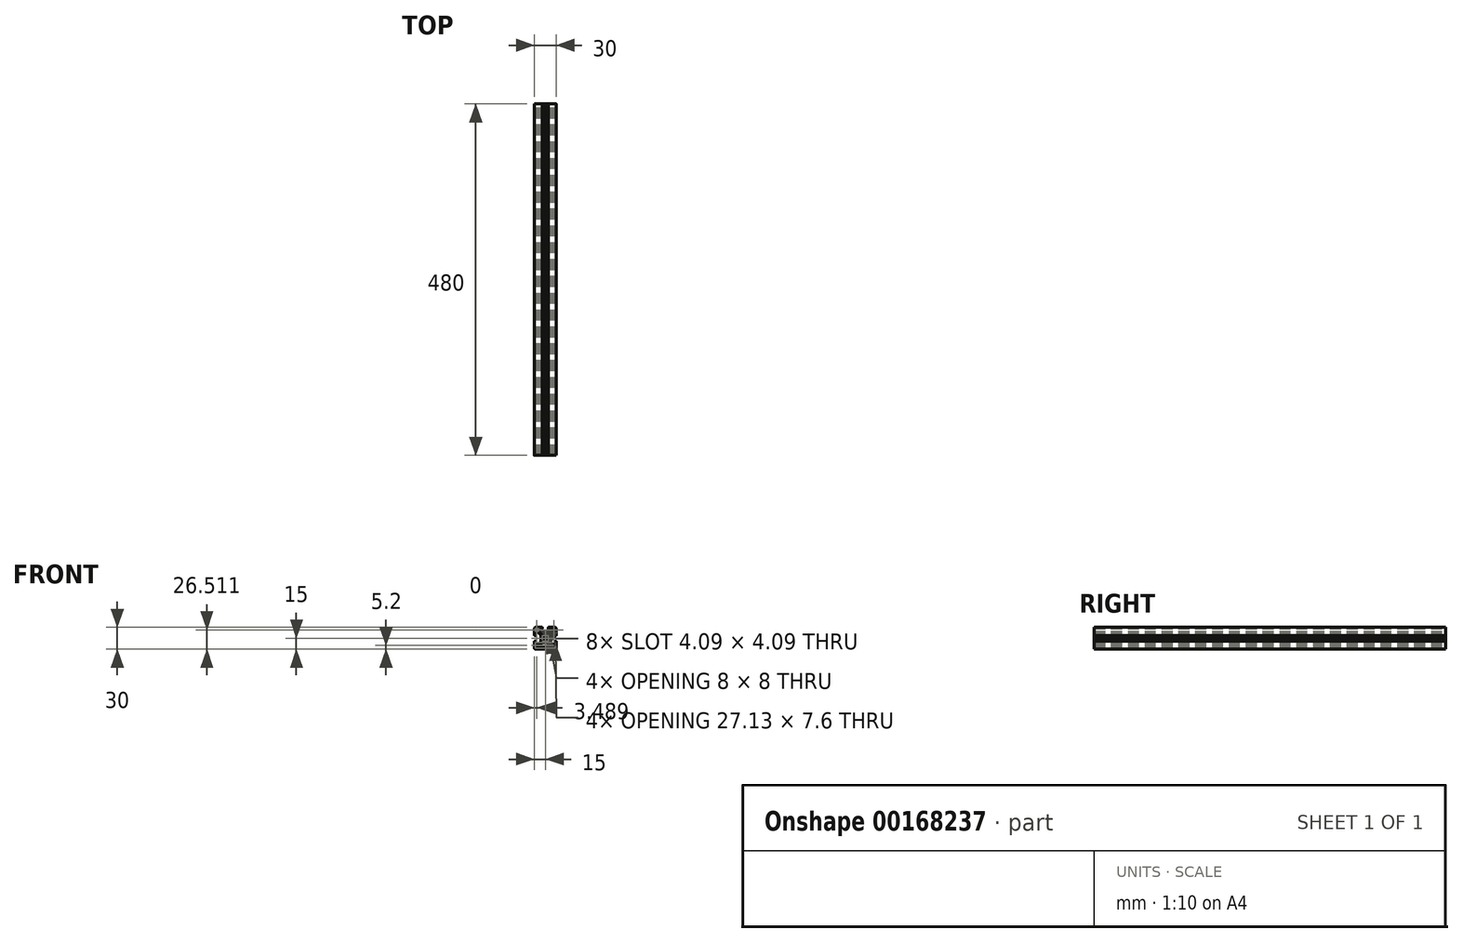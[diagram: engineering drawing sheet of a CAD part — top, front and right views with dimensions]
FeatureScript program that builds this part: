
annotation { "Feature Type Name" : "Feature", "Feature Type Description" : "" }
export const myFeature = defineFeature(function(context is Context, id is Id, definition is map)
    precondition{}
    {
        {
            var Q0;
            Q0=qCreatedBy(makeId("Front.planeOp"),FACE);
            var sketch = newSketch(context, id + "F0", { "sketchPlane" : qUnion([Q0])});
            skLineSegment(sketch, "E0", {"start": v(0, 17) * mm, "end": v(0, -17) * mm});
            skLineSegment(sketch, "E1", {"start": v(-17, 0) * mm, "end": v(17, 0) * mm});
            skLineSegment(sketch, "E2", {"start": v(-13, 15) * mm, "end": v(-4.3, 15) * mm});
            skLineSegment(sketch, "E3", {"start": v(-13, -15) * mm, "end": v(13, -15) * mm});
            skLineSegment(sketch, "E4", {"start": v(-15, 13) * mm, "end": v(-15, 4.3) * mm});
            skArc(sketch, "E5", {"start": v(15, 13) * mm, "mid": v(14.41, 14.41) * mm, "end": v(13, 15) * mm});
            skArc(sketch, "E6", {"start": v(-13, 15) * mm, "mid": v(-14.41, 14.41) * mm, "end": v(-15, 13) * mm});
            skArc(sketch, "E7", {"start": v(-15, -13) * mm, "mid": v(-14.41, -14.41) * mm, "end": v(-13, -15) * mm});
            skArc(sketch, "E8", {"start": v(13, -15) * mm, "mid": v(14.41, -14.41) * mm, "end": v(15, -13) * mm});
            skLineSegment(sketch, "E9", {"start": v(-13, -8.25) * mm, "end": v(-13, -4.3) * mm});
            skLineSegment(sketch, "E10", {"start": v(-8.08, -13) * mm, "end": v(8.08, -13) * mm});
            skLineSegment(sketch, "E11", {"start": v(-14.7, -4) * mm, "end": v(-13.3, -4) * mm});
            skLineSegment(sketch, "E12", {"start": v(-14.7, 4) * mm, "end": v(-13.3, 4) * mm});
            skLineSegment(sketch, "E13", {"start": v(-13, 4.3) * mm, "end": v(-13, 8.25) * mm});
            skLineSegment(sketch, "E14", {"start": v(4.3, 15) * mm, "end": v(13, 15) * mm});
            skLineSegment(sketch, "E15", {"start": v(-9.66, -8.25) * mm, "end": v(-13, -8.25) * mm});
            skLineSegment(sketch, "E16", {"start": v(-9.66, 8.25) * mm, "end": v(-13, 8.25) * mm});
            skLineSegment(sketch, "E17", {"start": v(4.59, 6) * mm, "end": v(0.65, 6) * mm});
            skLineSegment(sketch, "E18", {"start": v(4.17, -6) * mm, "end": v(-4.17, -6) * mm});
            skLineSegment(sketch, "E19", {"start": v(-6, -4.59) * mm, "end": v(-6, -2.5) * mm});
            skLineSegment(sketch, "E20", {"start": v(-4.59, 6) * mm, "end": v(-8.25, 9.66) * mm});
            skLineSegment(sketch, "E21", {"start": v(-6, 4.59) * mm, "end": v(-9.66, 8.25) * mm});
            skLineSegment(sketch, "E22", {"start": v(4.59, 6) * mm, "end": v(8.25, 9.66) * mm});
            skLineSegment(sketch, "E23", {"start": v(4.88, -6.3) * mm, "end": v(7.74, -9.16) * mm});
            skLineSegment(sketch, "E24", {"start": v(-4.88, -6.3) * mm, "end": v(-7.74, -9.16) * mm});
            skLineSegment(sketch, "E25", {"start": v(-6, -4.59) * mm, "end": v(-9.66, -8.25) * mm});
            skLineSegment(sketch, "E26", {"start": v(-15, -4.3) * mm, "end": v(-15, -13) * mm});
            skLineSegment(sketch, "E27", {"start": v(-4, 14.7) * mm, "end": v(-4, 13.3) * mm});
            skLineSegment(sketch, "E28", {"start": v(4, 14.7) * mm, "end": v(4, 13.3) * mm});
            skLineSegment(sketch, "E29", {"start": v(8.25, 9.66) * mm, "end": v(8.25, 13) * mm});
            skLineSegment(sketch, "E30", {"start": v(-8.25, 9.66) * mm, "end": v(-8.25, 13) * mm});
            skLineSegment(sketch, "E31", {"start": v(-4.3, 13) * mm, "end": v(-8.25, 13) * mm});
            skLineSegment(sketch, "E32", {"start": v(4.3, 13) * mm, "end": v(8.25, 13) * mm});
            skArc(sketch, "E33", {"start": v(-9.91, 12.35) * mm, "mid": v(-13.04, 13.04) * mm, "end": v(-12.35, 9.91) * mm});
            skLineSegment(sketch, "E34", {"start": v(-9.55, 11.34) * mm, "end": v(-9.91, 12.35) * mm});
            skLineSegment(sketch, "E35", {"start": v(-11.34, 9.55) * mm, "end": v(-12.35, 9.91) * mm});
            skArc(sketch, "E36", {"start": v(-11.34, 9.55) * mm, "mid": v(-9.87, 9.87) * mm, "end": v(-9.55, 11.34) * mm});
            skLineSegment(sketch, "E37", {"start": v(-8.45, -9.45) * mm, "end": v(-11.07, -9.45) * mm});
            skLineSegment(sketch, "E38", {"start": v(-11.07, -9.45) * mm, "end": v(-12.35, -9.91) * mm});
            skArc(sketch, "E39", {"start": v(-12.35, -9.91) * mm, "mid": v(-13.2, -12.86) * mm, "end": v(-10.14, -12.78) * mm});
            skArc(sketch, "E40", {"start": v(-8.5, -12.78) * mm, "mid": v(-9.31, -12.35) * mm, "end": v(-10.14, -12.78) * mm});
            skArc(sketch, "E41", {"start": v(-8.45, -9.45) * mm, "mid": v(-8.07, -9.37) * mm, "end": v(-7.74, -9.16) * mm});
            skArc(sketch, "E42", {"start": v(-4.17, -6) * mm, "mid": v(-4.55, -6.08) * mm, "end": v(-4.88, -6.3) * mm});
            skArc(sketch, "E43", {"start": v(4.88, -6.3) * mm, "mid": v(4.55, -6.08) * mm, "end": v(4.17, -6) * mm});
            skLineSegment(sketch, "E44", {"start": v(3.5, 4) * mm, "end": v(2, 4) * mm});
            skLineSegment(sketch, "E45", {"start": v(4, -3.5) * mm, "end": v(4, -2) * mm});
            skLineSegment(sketch, "E46", {"start": v(3.5, -4) * mm, "end": v(2, -4) * mm});
            skLineSegment(sketch, "E47", {"start": v(-4, -3.5) * mm, "end": v(-4, -2) * mm});
            skLineSegment(sketch, "E48", {"start": v(-2.5, 6) * mm, "end": v(-1.22, 5.75) * mm});
            skLineSegment(sketch, "E49", {"start": v(0, 5.7) * mm, "end": v(-0.4, 5.93) * mm});
            skLineSegment(sketch, "E50", {"start": v(0, 5.7) * mm, "end": v(0.4, 5.93) * mm});
            skLineSegment(sketch, "E51", {"start": v(-2.5, 6) * mm, "end": v(-4.59, 6) * mm});
            skArc(sketch, "E52", {"start": v(0.65, 6) * mm, "mid": v(0.52, 5.98) * mm, "end": v(0.4, 5.93) * mm});
            skArc(sketch, "E53", {"start": v(-0.4, 5.93) * mm, "mid": v(-0.65, 6) * mm, "end": v(-0.9, 5.93) * mm});
            skLineSegment(sketch, "E54", {"start": v(-1.22, 5.75) * mm, "end": v(-0.9, 5.93) * mm});
            skArc(sketch, "E55", {"start": v(-6, 0.65) * mm, "mid": v(-5.98, 0.52) * mm, "end": v(-5.93, 0.4) * mm});
            skLineSegment(sketch, "E56", {"start": v(-6, -2.5) * mm, "end": v(-5.75, -1.22) * mm});
            skLineSegment(sketch, "E57", {"start": v(-5.7, 0) * mm, "end": v(-5.93, -0.4) * mm});
            skLineSegment(sketch, "E58", {"start": v(-5.7, 0) * mm, "end": v(-5.93, 0.4) * mm});
            skArc(sketch, "E59", {"start": v(-5.93, -0.4) * mm, "mid": v(-6, -0.65) * mm, "end": v(-5.93, -0.9) * mm});
            skLineSegment(sketch, "E60", {"start": v(-5.75, -1.22) * mm, "end": v(-5.93, -0.9) * mm});
            skLineSegment(sketch, "E61", {"start": v(-6, 0.65) * mm, "end": v(-6, 4.59) * mm});
            skArc(sketch, "E62", {"start": v(4, 13.3) * mm, "mid": v(4.09, 13.09) * mm, "end": v(4.3, 13) * mm});
            skArc(sketch, "E63", {"start": v(4.3, 15) * mm, "mid": v(4.09, 14.91) * mm, "end": v(4, 14.7) * mm});
            skArc(sketch, "E64", {"start": v(-4.3, 13) * mm, "mid": v(-4.09, 13.09) * mm, "end": v(-4, 13.3) * mm});
            skArc(sketch, "E65", {"start": v(-4, 14.7) * mm, "mid": v(-4.09, 14.91) * mm, "end": v(-4.3, 15) * mm});
            skArc(sketch, "E66", {"start": v(-13.3, 4) * mm, "mid": v(-13.09, 4.09) * mm, "end": v(-13, 4.3) * mm});
            skArc(sketch, "E67", {"start": v(-15, 4.3) * mm, "mid": v(-14.91, 4.09) * mm, "end": v(-14.7, 4) * mm});
            skArc(sketch, "E68", {"start": v(-13, -4.3) * mm, "mid": v(-13.09, -4.09) * mm, "end": v(-13.3, -4) * mm});
            skArc(sketch, "E69", {"start": v(-14.7, -4) * mm, "mid": v(-14.91, -4.09) * mm, "end": v(-15, -4.3) * mm});
            skArc(sketch, "E70", {"start": v(0.99, 3.25) * mm, "mid": v(0, 3.4) * mm, "end": v(-0.99, 3.25) * mm});
            skArc(sketch, "E71", {"start": v(-1.5, 3.58) * mm, "mid": v(-1.32, 3.3) * mm, "end": v(-0.99, 3.25) * mm});
            skArc(sketch, "E72", {"start": v(-1.5, 3.58) * mm, "mid": v(-1.67, 3.88) * mm, "end": v(-2, 4) * mm});
            skArc(sketch, "E73", {"start": v(0.99, 3.25) * mm, "mid": v(1.32, 3.3) * mm, "end": v(1.5, 3.58) * mm});
            skArc(sketch, "E74", {"start": v(2, 4) * mm, "mid": v(1.67, 3.88) * mm, "end": v(1.5, 3.58) * mm});
            skLineSegment(sketch, "E75", {"start": v(-2, 4) * mm, "end": v(-3.5, 4) * mm});
            skArc(sketch, "E76", {"start": v(-3.5, 4) * mm, "mid": v(-3.85, 3.85) * mm, "end": v(-4, 3.5) * mm});
            skArc(sketch, "E77", {"start": v(4, 3.5) * mm, "mid": v(3.85, 3.85) * mm, "end": v(3.5, 4) * mm});
            skArc(sketch, "E78", {"start": v(3.5, -4) * mm, "mid": v(3.85, -3.85) * mm, "end": v(4, -3.5) * mm});
            skArc(sketch, "E79", {"start": v(-4, -3.5) * mm, "mid": v(-3.85, -3.85) * mm, "end": v(-3.5, -4) * mm});
            skArc(sketch, "E80", {"start": v(-3.25, 0.99) * mm, "mid": v(-3.4, 0) * mm, "end": v(-3.25, -0.99) * mm});
            skArc(sketch, "E81", {"start": v(-3.58, -1.5) * mm, "mid": v(-3.3, -1.32) * mm, "end": v(-3.25, -0.99) * mm});
            skArc(sketch, "E82", {"start": v(-3.58, -1.5) * mm, "mid": v(-3.88, -1.67) * mm, "end": v(-4, -2) * mm});
            skArc(sketch, "E83", {"start": v(-3.25, 0.99) * mm, "mid": v(-3.3, 1.32) * mm, "end": v(-3.58, 1.5) * mm});
            skArc(sketch, "E84", {"start": v(-4, 2) * mm, "mid": v(-3.88, 1.67) * mm, "end": v(-3.58, 1.5) * mm});
            skArc(sketch, "E85", {"start": v(3.25, -0.99) * mm, "mid": v(3.4, 0) * mm, "end": v(3.25, 0.99) * mm});
            skArc(sketch, "E86", {"start": v(3.58, 1.5) * mm, "mid": v(3.3, 1.32) * mm, "end": v(3.25, 0.99) * mm});
            skArc(sketch, "E87", {"start": v(3.58, 1.5) * mm, "mid": v(3.88, 1.67) * mm, "end": v(4, 2) * mm});
            skArc(sketch, "E88", {"start": v(3.25, -0.99) * mm, "mid": v(3.3, -1.32) * mm, "end": v(3.58, -1.5) * mm});
            skArc(sketch, "E89", {"start": v(4, -2) * mm, "mid": v(3.88, -1.67) * mm, "end": v(3.58, -1.5) * mm});
            skArc(sketch, "E90", {"start": v(-0.99, -3.25) * mm, "mid": v(0, -3.4) * mm, "end": v(0.99, -3.25) * mm});
            skArc(sketch, "E91", {"start": v(-0.99, -3.25) * mm, "mid": v(-1.32, -3.3) * mm, "end": v(-1.5, -3.58) * mm});
            skArc(sketch, "E92", {"start": v(-2, -4) * mm, "mid": v(-1.67, -3.88) * mm, "end": v(-1.5, -3.58) * mm});
            skArc(sketch, "E93", {"start": v(1.5, -3.58) * mm, "mid": v(1.32, -3.3) * mm, "end": v(0.99, -3.25) * mm});
            skArc(sketch, "E94", {"start": v(1.5, -3.58) * mm, "mid": v(1.67, -3.88) * mm, "end": v(2, -4) * mm});
            skLineSegment(sketch, "E95", {"start": v(4, 2) * mm, "end": v(4, 3.5) * mm});
            skLineSegment(sketch, "E96", {"start": v(-2, -4) * mm, "end": v(-3.5, -4) * mm});
            skLineSegment(sketch, "E97", {"start": v(-4, 2) * mm, "end": v(-4, 3.5) * mm});
            skCircle(sketch, "E98", {"center": v(0, 0) * mm, "radius": 3.4 * mm});
            skLineSegment(sketch, "E99", {"start": v(-11.7, -7.8) * mm, "end": v(-11.7, -15.6) * mm});
            skLineSegment(sketch, "E100", {"start": v(-15.6, -11.7) * mm, "end": v(-7.8, -11.7) * mm});
            skLineSegment(sketch, "E101", {"start": v(-11.7, 15.6) * mm, "end": v(-11.7, 7.8) * mm});
            skLineSegment(sketch, "E102", {"start": v(-15.6, 11.7) * mm, "end": v(-7.8, 11.7) * mm});
            skArc(sketch, "E103", {"start": v(7.74, -9.16) * mm, "mid": v(8.07, -9.37) * mm, "end": v(8.45, -9.45) * mm});
            skArc(sketch, "E104", {"start": v(12.35, 9.91) * mm, "mid": v(13.04, 13.04) * mm, "end": v(9.91, 12.35) * mm});
            skLineSegment(sketch, "E105", {"start": v(9.55, 11.34) * mm, "end": v(9.91, 12.35) * mm});
            skLineSegment(sketch, "E106", {"start": v(11.34, 9.55) * mm, "end": v(12.35, 9.91) * mm});
            skArc(sketch, "E107", {"start": v(9.55, 11.34) * mm, "mid": v(9.87, 9.87) * mm, "end": v(11.34, 9.55) * mm});
            skLineSegment(sketch, "E108", {"start": v(8.45, -9.45) * mm, "end": v(11.07, -9.45) * mm});
            skLineSegment(sketch, "E109", {"start": v(11.07, -9.45) * mm, "end": v(12.35, -9.91) * mm});
            skArc(sketch, "E110", {"start": v(10.14, -12.78) * mm, "mid": v(13.2, -12.86) * mm, "end": v(12.35, -9.91) * mm});
            skArc(sketch, "E111", {"start": v(10.14, -12.78) * mm, "mid": v(9.31, -12.35) * mm, "end": v(8.5, -12.78) * mm});
            skLineSegment(sketch, "E112", {"start": v(11.7, -7.8) * mm, "end": v(11.7, -15.6) * mm});
            skLineSegment(sketch, "E113", {"start": v(15.6, -11.7) * mm, "end": v(7.8, -11.7) * mm});
            skLineSegment(sketch, "E114", {"start": v(11.7, 15.6) * mm, "end": v(11.7, 7.8) * mm});
            skLineSegment(sketch, "E115", {"start": v(15.6, 11.7) * mm, "end": v(7.8, 11.7) * mm});
            skLineSegment(sketch, "E116", {"start": v(15, 13) * mm, "end": v(15, 4.3) * mm});
            skLineSegment(sketch, "E117", {"start": v(15, -4.3) * mm, "end": v(15, -13) * mm});
            skLineSegment(sketch, "E118", {"start": v(13, -8.25) * mm, "end": v(13, -4.3) * mm});
            skLineSegment(sketch, "E119", {"start": v(13, 4.3) * mm, "end": v(13, 8.25) * mm});
            skLineSegment(sketch, "E120", {"start": v(14.7, -4) * mm, "end": v(13.3, -4) * mm});
            skArc(sketch, "E121", {"start": v(13.3, -4) * mm, "mid": v(13.09, -4.09) * mm, "end": v(13, -4.3) * mm});
            skLineSegment(sketch, "E122", {"start": v(14.7, 4) * mm, "end": v(13.3, 4) * mm});
            skArc(sketch, "E123", {"start": v(14.7, 4) * mm, "mid": v(14.91, 4.09) * mm, "end": v(15, 4.3) * mm});
            skArc(sketch, "E124", {"start": v(13, 4.3) * mm, "mid": v(13.09, 4.09) * mm, "end": v(13.3, 4) * mm});
            skLineSegment(sketch, "E125", {"start": v(9.66, 8.25) * mm, "end": v(13, 8.25) * mm});
            skLineSegment(sketch, "E126", {"start": v(9.66, -8.25) * mm, "end": v(13, -8.25) * mm});
            skLineSegment(sketch, "E127", {"start": v(6, 4.59) * mm, "end": v(9.66, 8.25) * mm});
            skLineSegment(sketch, "E128", {"start": v(6, -4.59) * mm, "end": v(9.66, -8.25) * mm});
            skArc(sketch, "E129", {"start": v(15, -4.3) * mm, "mid": v(14.91, -4.09) * mm, "end": v(14.7, -4) * mm});
            skLineSegment(sketch, "E130", {"start": v(6, 4.59) * mm, "end": v(6, 2.5) * mm});
            skLineSegment(sketch, "E131", {"start": v(6, -0.65) * mm, "end": v(6, -4.59) * mm});
            skArc(sketch, "E132", {"start": v(6, -0.65) * mm, "mid": v(5.98, -0.52) * mm, "end": v(5.93, -0.4) * mm});
            skLineSegment(sketch, "E133", {"start": v(6, 2.5) * mm, "end": v(5.75, 1.22) * mm});
            skLineSegment(sketch, "E134", {"start": v(5.7, 0) * mm, "end": v(5.93, 0.4) * mm});
            skLineSegment(sketch, "E135", {"start": v(5.7, 0) * mm, "end": v(5.93, -0.4) * mm});
            skArc(sketch, "E136", {"start": v(5.93, 0.4) * mm, "mid": v(6, 0.65) * mm, "end": v(5.93, 0.9) * mm});
            skLineSegment(sketch, "E137", {"start": v(5.75, 1.22) * mm, "end": v(5.93, 0.9) * mm});
            skArc(sketch, "E138", {"start": v(8.08, -13) * mm, "mid": v(8.31, -12.94) * mm, "end": v(8.5, -12.78) * mm});
            skArc(sketch, "E139", {"start": v(-8.5, -12.78) * mm, "mid": v(-8.31, -12.94) * mm, "end": v(-8.08, -13) * mm});
            skSolve(sketch);
        }
        {
            var Q0;
            Q0=qCreatedBy(makeId("Front.planeOp"),FACE);
            var sketch = newSketch(context, id + "F1", { "sketchPlane" : qUnion([Q0])});
            skLineSegment(sketch, "E140.0", {"start": v(4.59, 6) * mm, "end": v(0.65, 6) * mm});
            skLineSegment(sketch, "E140.2", {"start": v(6, 4.59) * mm, "end": v(6, 2.5) * mm});
            skLineSegment(sketch, "E140.5", {"start": v(6, -0.65) * mm, "end": v(6, -4.59) * mm});
            skLineSegment(sketch, "E140.7", {"start": v(4.3, 13) * mm, "end": v(8.25, 13) * mm});
            skLineSegment(sketch, "E140.8", {"start": v(-15, 13) * mm, "end": v(-15, 4.3) * mm});
            skLineSegment(sketch, "E140.11", {"start": v(6, -4.59) * mm, "end": v(9.66, -8.25) * mm});
            skArc(sketch, "E140.12", {"start": v(-9.91, 12.35) * mm, "mid": v(-13.04, 13.04) * mm, "end": v(-12.35, 9.91) * mm});
            skLineSegment(sketch, "E140.13", {"start": v(4.17, -6) * mm, "end": v(-4.17, -6) * mm});
            skLineSegment(sketch, "E140.14", {"start": v(-2.5, 6) * mm, "end": v(-4.59, 6) * mm});
            skArc(sketch, "E140.15", {"start": v(15, 13) * mm, "mid": v(14.41, 14.41) * mm, "end": v(13, 15) * mm});
            skLineSegment(sketch, "E140.16", {"start": v(-8.08, -13) * mm, "end": v(8.08, -13) * mm});
            skLineSegment(sketch, "E140.17", {"start": v(-13, -8.25) * mm, "end": v(-13, -4.3) * mm});
            skArc(sketch, "E140.18", {"start": v(-15, -13) * mm, "mid": v(-14.41, -14.41) * mm, "end": v(-13, -15) * mm});
            skArc(sketch, "E140.19", {"start": v(13, -15) * mm, "mid": v(14.41, -14.41) * mm, "end": v(15, -13) * mm});
            skArc(sketch, "E140.20", {"start": v(-13, 15) * mm, "mid": v(-14.41, 14.41) * mm, "end": v(-15, 13) * mm});
            skLineSegment(sketch, "E140.21", {"start": v(15, 13) * mm, "end": v(15, 4.3) * mm});
            skLineSegment(sketch, "E140.22", {"start": v(-13, 15) * mm, "end": v(-4.3, 15) * mm});
            skLineSegment(sketch, "E140.23", {"start": v(-13, -15) * mm, "end": v(13, -15) * mm});
            skLineSegment(sketch, "E140.26", {"start": v(-9.66, -8.25) * mm, "end": v(-13, -8.25) * mm});
            skLineSegment(sketch, "E140.27", {"start": v(4.3, 15) * mm, "end": v(13, 15) * mm});
            skLineSegment(sketch, "E140.28", {"start": v(-4.3, 13) * mm, "end": v(-8.25, 13) * mm});
            skLineSegment(sketch, "E140.29", {"start": v(6, 4.59) * mm, "end": v(9.66, 8.25) * mm});
            skLineSegment(sketch, "E140.30", {"start": v(-13, 4.3) * mm, "end": v(-13, 8.25) * mm});
            skLineSegment(sketch, "E140.31", {"start": v(-6, -4.59) * mm, "end": v(-6, -2.5) * mm});
            skArc(sketch, "E140.32", {"start": v(-11.34, 9.55) * mm, "mid": v(-9.87, 9.87) * mm, "end": v(-9.55, 11.34) * mm});
            skArc(sketch, "E140.33", {"start": v(10.14, -12.78) * mm, "mid": v(13.2, -12.86) * mm, "end": v(12.35, -9.91) * mm});
            skLineSegment(sketch, "E140.34", {"start": v(8.45, -9.45) * mm, "end": v(11.07, -9.45) * mm});
            skLineSegment(sketch, "E140.35", {"start": v(-8.25, 9.66) * mm, "end": v(-8.25, 13) * mm});
            skLineSegment(sketch, "E140.36", {"start": v(9.66, -8.25) * mm, "end": v(13, -8.25) * mm});
            skLineSegment(sketch, "E140.37", {"start": v(8.25, 9.66) * mm, "end": v(8.25, 13) * mm});
            skLineSegment(sketch, "E140.38", {"start": v(-6, 0.65) * mm, "end": v(-6, 4.59) * mm});
            skArc(sketch, "E140.39", {"start": v(9.55, 11.34) * mm, "mid": v(9.87, 9.87) * mm, "end": v(11.34, 9.55) * mm});
            skLineSegment(sketch, "E140.40", {"start": v(9.66, 8.25) * mm, "end": v(13, 8.25) * mm});
            skLineSegment(sketch, "E140.41", {"start": v(-4.59, 6) * mm, "end": v(-8.25, 9.66) * mm});
            skLineSegment(sketch, "E140.42", {"start": v(-15, -4.3) * mm, "end": v(-15, -13) * mm});
            skLineSegment(sketch, "E140.43", {"start": v(-6, -4.59) * mm, "end": v(-9.66, -8.25) * mm});
            skArc(sketch, "E140.44", {"start": v(12.35, 9.91) * mm, "mid": v(13.04, 13.04) * mm, "end": v(9.91, 12.35) * mm});
            skLineSegment(sketch, "E140.45", {"start": v(-4.88, -6.3) * mm, "end": v(-7.74, -9.16) * mm});
            skLineSegment(sketch, "E140.46", {"start": v(13, -8.25) * mm, "end": v(13, -4.3) * mm});
            skArc(sketch, "E140.48", {"start": v(-12.35, -9.91) * mm, "mid": v(-13.2, -12.86) * mm, "end": v(-10.14, -12.78) * mm});
            skLineSegment(sketch, "E140.49", {"start": v(13, 4.3) * mm, "end": v(13, 8.25) * mm});
            skLineSegment(sketch, "E140.50", {"start": v(4.88, -6.3) * mm, "end": v(7.74, -9.16) * mm});
            skLineSegment(sketch, "E140.51", {"start": v(4.59, 6) * mm, "end": v(8.25, 9.66) * mm});
            skLineSegment(sketch, "E140.52", {"start": v(-8.45, -9.45) * mm, "end": v(-11.07, -9.45) * mm});
            skLineSegment(sketch, "E140.53", {"start": v(-6, 4.59) * mm, "end": v(-9.66, 8.25) * mm});
            skLineSegment(sketch, "E140.54", {"start": v(15, -4.3) * mm, "end": v(15, -13) * mm});
            skLineSegment(sketch, "E140.57", {"start": v(-9.66, 8.25) * mm, "end": v(-13, 8.25) * mm});
            skArc(sketch, "E140.58", {"start": v(-0.99, -3.25) * mm, "mid": v(0, -3.4) * mm, "end": v(0.99, -3.25) * mm});
            skArc(sketch, "E140.59", {"start": v(0.99, 3.25) * mm, "mid": v(0, 3.4) * mm, "end": v(-0.99, 3.25) * mm});
            skLineSegment(sketch, "E140.60", {"start": v(-11.34, 9.55) * mm, "end": v(-12.35, 9.91) * mm});
            skArc(sketch, "E140.61", {"start": v(-3.58, -1.5) * mm, "mid": v(-3.3, -1.32) * mm, "end": v(-3.25, -0.99) * mm});
            skLineSegment(sketch, "E140.62", {"start": v(-9.55, 11.34) * mm, "end": v(-9.91, 12.35) * mm});
            skLineSegment(sketch, "E140.63", {"start": v(-2.5, 6) * mm, "end": v(-1.22, 5.75) * mm});
            skLineSegment(sketch, "E140.64", {"start": v(-2, -4) * mm, "end": v(-3.5, -4) * mm});
            skLineSegment(sketch, "E140.65", {"start": v(-4, 2) * mm, "end": v(-4, 3.5) * mm});
            skArc(sketch, "E140.66", {"start": v(-3.25, 0.99) * mm, "mid": v(-3.4, 0) * mm, "end": v(-3.25, -0.99) * mm});
            skArc(sketch, "E140.67", {"start": v(-3.58, -1.5) * mm, "mid": v(-3.88, -1.67) * mm, "end": v(-4, -2) * mm});
            skLineSegment(sketch, "E140.68", {"start": v(4, 2) * mm, "end": v(4, 3.5) * mm});
            skArc(sketch, "E140.69", {"start": v(6, -0.65) * mm, "mid": v(5.98, -0.52) * mm, "end": v(5.93, -0.4) * mm});
            skArc(sketch, "E140.70", {"start": v(10.14, -12.78) * mm, "mid": v(9.31, -12.35) * mm, "end": v(8.5, -12.78) * mm});
            skArc(sketch, "E140.71", {"start": v(-4, -3.5) * mm, "mid": v(-3.85, -3.85) * mm, "end": v(-3.5, -4) * mm});
            skLineSegment(sketch, "E140.72", {"start": v(-4, -3.5) * mm, "end": v(-4, -2) * mm});
            skArc(sketch, "E140.73", {"start": v(1.5, -3.58) * mm, "mid": v(1.67, -3.88) * mm, "end": v(2, -4) * mm});
            skLineSegment(sketch, "E140.74", {"start": v(3.5, 4) * mm, "end": v(2, 4) * mm});
            skLineSegment(sketch, "E140.75", {"start": v(3.5, -4) * mm, "end": v(2, -4) * mm});
            skArc(sketch, "E140.76", {"start": v(3.5, -4) * mm, "mid": v(3.85, -3.85) * mm, "end": v(4, -3.5) * mm});
            skArc(sketch, "E140.77", {"start": v(-3.5, 4) * mm, "mid": v(-3.85, 3.85) * mm, "end": v(-4, 3.5) * mm});
            skLineSegment(sketch, "E140.78", {"start": v(4, -3.5) * mm, "end": v(4, -2) * mm});
            skArc(sketch, "E140.79", {"start": v(4, 3.5) * mm, "mid": v(3.85, 3.85) * mm, "end": v(3.5, 4) * mm});
            skLineSegment(sketch, "E140.80", {"start": v(-2, 4) * mm, "end": v(-3.5, 4) * mm});
            skArc(sketch, "E140.81", {"start": v(-8.5, -12.78) * mm, "mid": v(-8.31, -12.94) * mm, "end": v(-8.08, -13) * mm});
            skLineSegment(sketch, "E140.82", {"start": v(11.07, -9.45) * mm, "end": v(12.35, -9.91) * mm});
            skArc(sketch, "E140.83", {"start": v(4.88, -6.3) * mm, "mid": v(4.55, -6.08) * mm, "end": v(4.17, -6) * mm});
            skArc(sketch, "E140.84", {"start": v(8.08, -13) * mm, "mid": v(8.31, -12.94) * mm, "end": v(8.5, -12.78) * mm});
            skArc(sketch, "E140.85", {"start": v(-4, 2) * mm, "mid": v(-3.88, 1.67) * mm, "end": v(-3.58, 1.5) * mm});
            skArc(sketch, "E140.86", {"start": v(-4.17, -6) * mm, "mid": v(-4.55, -6.08) * mm, "end": v(-4.88, -6.3) * mm});
            skLineSegment(sketch, "E140.87", {"start": v(11.34, 9.55) * mm, "end": v(12.35, 9.91) * mm});
            skArc(sketch, "E140.88", {"start": v(-8.45, -9.45) * mm, "mid": v(-8.07, -9.37) * mm, "end": v(-7.74, -9.16) * mm});
            skLineSegment(sketch, "E140.89", {"start": v(9.55, 11.34) * mm, "end": v(9.91, 12.35) * mm});
            skArc(sketch, "E140.90", {"start": v(4, -2) * mm, "mid": v(3.88, -1.67) * mm, "end": v(3.58, -1.5) * mm});
            skArc(sketch, "E140.91", {"start": v(-1.5, 3.58) * mm, "mid": v(-1.67, 3.88) * mm, "end": v(-2, 4) * mm});
            skArc(sketch, "E140.92", {"start": v(-8.5, -12.78) * mm, "mid": v(-9.31, -12.35) * mm, "end": v(-10.14, -12.78) * mm});
            skArc(sketch, "E140.93", {"start": v(3.25, -0.99) * mm, "mid": v(3.3, -1.32) * mm, "end": v(3.58, -1.5) * mm});
            skLineSegment(sketch, "E140.94", {"start": v(-6, -2.5) * mm, "end": v(-5.75, -1.22) * mm});
            skArc(sketch, "E140.95", {"start": v(-1.5, 3.58) * mm, "mid": v(-1.32, 3.3) * mm, "end": v(-0.99, 3.25) * mm});
            skLineSegment(sketch, "E140.96", {"start": v(-11.07, -9.45) * mm, "end": v(-12.35, -9.91) * mm});
            skArc(sketch, "E140.97", {"start": v(7.74, -9.16) * mm, "mid": v(8.07, -9.37) * mm, "end": v(8.45, -9.45) * mm});
            skArc(sketch, "E140.98", {"start": v(3.58, 1.5) * mm, "mid": v(3.88, 1.67) * mm, "end": v(4, 2) * mm});
            skArc(sketch, "E140.99", {"start": v(3.58, 1.5) * mm, "mid": v(3.3, 1.32) * mm, "end": v(3.25, 0.99) * mm});
            skArc(sketch, "E140.100", {"start": v(3.25, -0.99) * mm, "mid": v(3.4, 0) * mm, "end": v(3.25, 0.99) * mm});
            skLineSegment(sketch, "E140.101", {"start": v(6, 2.5) * mm, "end": v(5.75, 1.22) * mm});
            skArc(sketch, "E140.102", {"start": v(15, -4.3) * mm, "mid": v(14.91, -4.09) * mm, "end": v(14.7, -4) * mm});
            skArc(sketch, "E140.103", {"start": v(-15, 4.3) * mm, "mid": v(-14.91, 4.09) * mm, "end": v(-14.7, 4) * mm});
            skLineSegment(sketch, "E140.104", {"start": v(-14.7, 4) * mm, "end": v(-13.3, 4) * mm});
            skLineSegment(sketch, "E140.105", {"start": v(0, 5.7) * mm, "end": v(-0.4, 5.93) * mm});
            skLineSegment(sketch, "E140.106", {"start": v(0, 5.7) * mm, "end": v(0.4, 5.93) * mm});
            skArc(sketch, "E140.107", {"start": v(-4, 14.7) * mm, "mid": v(-4.09, 14.91) * mm, "end": v(-4.3, 15) * mm});
            skArc(sketch, "E140.108", {"start": v(-13.3, 4) * mm, "mid": v(-13.09, 4.09) * mm, "end": v(-13, 4.3) * mm});
            skLineSegment(sketch, "E140.109", {"start": v(-14.7, -4) * mm, "end": v(-13.3, -4) * mm});
            skArc(sketch, "E140.110", {"start": v(-3.25, 0.99) * mm, "mid": v(-3.3, 1.32) * mm, "end": v(-3.58, 1.5) * mm});
            skArc(sketch, "E140.111", {"start": v(13, 4.3) * mm, "mid": v(13.09, 4.09) * mm, "end": v(13.3, 4) * mm});
            skArc(sketch, "E140.112", {"start": v(-2, -4) * mm, "mid": v(-1.67, -3.88) * mm, "end": v(-1.5, -3.58) * mm});
            skArc(sketch, "E140.113", {"start": v(14.7, 4) * mm, "mid": v(14.91, 4.09) * mm, "end": v(15, 4.3) * mm});
            skArc(sketch, "E140.114", {"start": v(-0.99, -3.25) * mm, "mid": v(-1.32, -3.3) * mm, "end": v(-1.5, -3.58) * mm});
            skArc(sketch, "E140.115", {"start": v(1.5, -3.58) * mm, "mid": v(1.32, -3.3) * mm, "end": v(0.99, -3.25) * mm});
            skArc(sketch, "E140.116", {"start": v(2, 4) * mm, "mid": v(1.67, 3.88) * mm, "end": v(1.5, 3.58) * mm});
            skArc(sketch, "E140.117", {"start": v(-13, -4.3) * mm, "mid": v(-13.09, -4.09) * mm, "end": v(-13.3, -4) * mm});
            skLineSegment(sketch, "E140.118", {"start": v(14.7, 4) * mm, "end": v(13.3, 4) * mm});
            skLineSegment(sketch, "E140.119", {"start": v(5.75, 1.22) * mm, "end": v(5.93, 0.9) * mm});
            skArc(sketch, "E140.120", {"start": v(0.99, 3.25) * mm, "mid": v(1.32, 3.3) * mm, "end": v(1.5, 3.58) * mm});
            skArc(sketch, "E140.121", {"start": v(13.3, -4) * mm, "mid": v(13.09, -4.09) * mm, "end": v(13, -4.3) * mm});
            skArc(sketch, "E140.122", {"start": v(5.93, 0.4) * mm, "mid": v(6, 0.65) * mm, "end": v(5.93, 0.9) * mm});
            skLineSegment(sketch, "E140.123", {"start": v(14.7, -4) * mm, "end": v(13.3, -4) * mm});
            skLineSegment(sketch, "E140.124", {"start": v(5.7, 0) * mm, "end": v(5.93, -0.4) * mm});
            skLineSegment(sketch, "E140.125", {"start": v(5.7, 0) * mm, "end": v(5.93, 0.4) * mm});
            skLineSegment(sketch, "E140.126", {"start": v(-1.22, 5.75) * mm, "end": v(-0.9, 5.93) * mm});
            skArc(sketch, "E140.127", {"start": v(-14.7, -4) * mm, "mid": v(-14.91, -4.09) * mm, "end": v(-15, -4.3) * mm});
            skArc(sketch, "E140.128", {"start": v(-4.3, 13) * mm, "mid": v(-4.09, 13.09) * mm, "end": v(-4, 13.3) * mm});
            skArc(sketch, "E140.129", {"start": v(4.3, 15) * mm, "mid": v(4.09, 14.91) * mm, "end": v(4, 14.7) * mm});
            skLineSegment(sketch, "E140.130", {"start": v(4, 14.7) * mm, "end": v(4, 13.3) * mm});
            skArc(sketch, "E140.131", {"start": v(4, 13.3) * mm, "mid": v(4.09, 13.09) * mm, "end": v(4.3, 13) * mm});
            skLineSegment(sketch, "E140.132", {"start": v(-4, 14.7) * mm, "end": v(-4, 13.3) * mm});
            skArc(sketch, "E140.133", {"start": v(0.65, 6) * mm, "mid": v(0.52, 5.98) * mm, "end": v(0.4, 5.93) * mm});
            skArc(sketch, "E140.134", {"start": v(-0.4, 5.93) * mm, "mid": v(-0.65, 6) * mm, "end": v(-0.9, 5.93) * mm});
            skLineSegment(sketch, "E140.135", {"start": v(-5.75, -1.22) * mm, "end": v(-5.93, -0.9) * mm});
            skArc(sketch, "E140.136", {"start": v(-5.93, -0.4) * mm, "mid": v(-6, -0.65) * mm, "end": v(-5.93, -0.9) * mm});
            skLineSegment(sketch, "E140.137", {"start": v(-5.7, 0) * mm, "end": v(-5.93, 0.4) * mm});
            skArc(sketch, "E140.138", {"start": v(-6, 0.65) * mm, "mid": v(-5.98, 0.52) * mm, "end": v(-5.93, 0.4) * mm});
            skLineSegment(sketch, "E140.139", {"start": v(-5.7, 0) * mm, "end": v(-5.93, -0.4) * mm});
            skSolve(sketch);
        }
        {
            var Q0;
            Q0=makeQuery(id+"F1.imprint","IMPRINT",FACE,{"disambiguationData":[TD([[makeQuery(id+"F1.imprint","IMPRINT",EDGE,{"derivedFrom":sQuery(id+"F1.wireOp",EDGE,"E140.0")}),1.0]])]});
            extrude(context, id + "F2", {"entities" : qUnion([Q0]), "endBound" : BoundingType.SYMMETRIC, "depth" : 480 * mm});
        }
    });
